# Revit family: Sanitary_Taps&Mixers_Zurn_Z81104-XL
name_source: partatom
category: Plumbing Fixtures
units: mm (PartAtom-declared; Revit-internal decimal feet)

## family parameters
Cut with Voids When Loaded = No
Host = Face
Maintain Annotation Orientation = No
OmniClass Number = 23.45.55.14
OmniClass Title = Single Faucets
Part Type = Normal
Room Calculation Point = No
Round Connector Dimension = Use Diameter
Shared = No

## types (11) — shared parameters
ADA Compliance = Yes
Assembly Code = D2010.60
CW Connection = Yes
CWFU = 1
Default Elevation = 48"
Description = Lavatory Faucet
Distance B/W Base & Aerator = 2 1/8"
Distance Between Centerset = 4"
HW Connection = Yes
HWFU = 1
Inlet Connection Size (inch) = 1/2"
Lead- Free Compliant = Yes
Main Material = Brass_Zurn_ Chrome Polished
Manufacturer = Zurn Water, LLC
Manufacturer Brand = Zurn
Model = Z81104-XL
Modified Date = 08/07/2025
Product Documentation Link = https://files.zurn.com
Product Installation Sheet URL = https://files.zurn.com
Product Page URL = https://www.zurn.com
Product data URL = https://www.bimobject.com
Spout Base Width = 6"
Spout Reach = 4 1/4"
URL = https://www.zurn.com
Vent Connection = No
Waste Connection = No
Width of Handle = 4"
zero-valued in all types: WFU

## per-type parameters (varying)
| type | Flow Rate | Type of Outlet | Water Sense Compliance |
| Z81104-XL-2M (2.2 GPM AERATOR OUTLET) | 2 GPM | AERATOR | No |
| Z81104-XL-3M (0.5 GPM SPRAY OUTLET) | 1 GPM | SPRAY | No |
| Z81104-XL-7M (1.0 GPM SPRAY OUTLET) | 1 GPM | SPRAY | Yes |
| Z81104-XL-16M (1.0 GPM SPRAY OUTLET) | 1 GPM | SPRAY | No |
| Z81104-XL-17M (1.5 GPM AREATOR OUTLET) | 2 GPM | AERATOR | Yes |
| Z81104-XL-22M (1.0 GPM LAMINAR OUTLET) | 1 GPM | LAMINAR | No |
| Z81104-XL-25M (0.35 GPM SPRAY OUTLET) | 0 GPM | SPRAY | No |
| Z81104-XL-27M (0.5 GPM LAMINAR OUTLET) | 1 GPM | LAMINAR | No |
| Z81104-XL-28M (0.5 GPM LAMINAR OUTLET) | 1 GPM | LAMINAR | No |
| Z81104-XL-4M (2.2 GPM LAMINAR OUTLET) | 2 GPM | LAMINAR | No |
| Z81104-XL-18M (1.5 GPM LAMINAR OUTLET) | 2 GPM | LAMINAR | Yes |

## geometry (parser evidence)
native form markers: Sweep x23
no freeform markers — native parametric forms only
